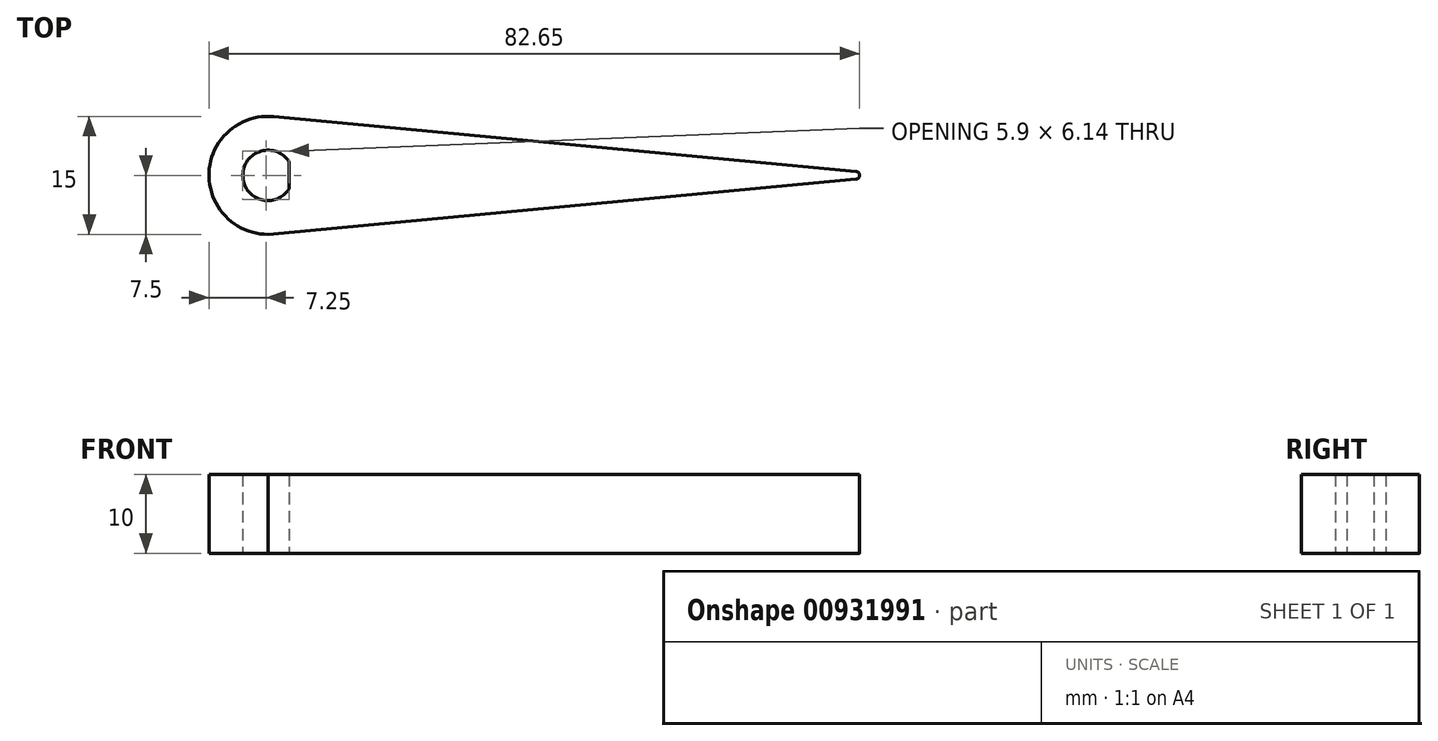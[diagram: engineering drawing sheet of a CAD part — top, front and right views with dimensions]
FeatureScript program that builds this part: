
annotation { "Feature Type Name" : "Feature", "Feature Type Description" : "" }
export const myFeature = defineFeature(function(context is Context, id is Id, definition is map)
    precondition{}
    {
        {
            var Q0;
            Q0=qCreatedBy(makeId("Top.planeOp"),FACE);
            var sketch = newSketch(context, id + "F0", { "sketchPlane" : qUnion([Q0])});
            skArc(sketch, "E0", {"start": v(2.7, 1.72) * mm, "mid": v(-3.2, 0) * mm, "end": v(2.7, -1.72) * mm});
            skLineSegment(sketch, "E1", {"start": v(2.7, 1.72) * mm, "end": v(2.7, -1.72) * mm});
            skCircle(sketch, "E2", {"center": v(0, 0) * mm, "radius": 7.5 * mm});
            skLineSegment(sketch, "E3", {"start": v(0, 0) * mm, "end": v(80, 0) * mm});
            skLineSegment(sketch, "E4", {"start": v(80, 0) * mm, "end": v(0, 7.53) * mm});
            skLineSegment(sketch, "E5", {"start": v(0, 7.53) * mm, "end": v(0, -7.5) * mm, "construction": true});
            skLineSegment(sketch, "E6", {"start": v(0, -7.5) * mm, "end": v(80, 0) * mm});
            skSolve(sketch);
        }
        {
            var Q0;
            {var subQ4=sQuery(id+"F0.wireOp",EDGE,"E0");Q0=makeQuery(id+"F0.imprint","IMPRINT",FACE,{"disambiguationData":[TD([[makeQuery(id+"F0.imprint","IMPRINT",EDGE,{"derivedFrom":subQ4}),-1.0]])]});}
            var Q1;
            {var subQ0=sQuery(id+"F0.wireOp",EDGE,"E4");var subQ1=sQuery(id+"F0.wireOp",EDGE,"E2");var subQ2=makeQuery(id+"F0.imprint","INTERSECT",VERTEX,{"derivedFrom":[subQ1,subQ0]});Q1=makeQuery(id+"F0.imprint","IMPRINT",FACE,{"disambiguationData":[TD([[makeQuery(id+"F0.imprint","IMPRINT",EDGE,{"disambiguationData":[TD([[subQ2,1.0]])],"derivedFrom":subQ1}),-1.0]])]});}
            var Q2;
            {var subQ0=sQuery(id+"F0.wireOp",EDGE,"E3");var subQ1=sQuery(id+"F0.wireOp",EDGE,"E2");var subQ2=makeQuery(id+"F0.imprint","INTERSECT",VERTEX,{"derivedFrom":[subQ1,subQ0]});Q2=makeQuery(id+"F0.imprint","IMPRINT",FACE,{"disambiguationData":[TD([[makeQuery(id+"F0.imprint","IMPRINT",EDGE,{"disambiguationData":[TD([[subQ2,1.0]])],"derivedFrom":subQ1}),-1.0]])]});}
            extrude(context, id + "F1", {"entities" : qUnion([Q0, Q1, Q2]), "depth" : 10 * mm, "offsetDistance" : 25 * mm});
        }
        {
            var Q0;
            Q0=makeQuery(id+"F1.opExtrude","SWEPT_EDGE",EDGE,{"disambiguationData":[OSD([sQuery(id+"F0.wireOp",EDGE,"E3"),sQuery(id+"F0.wireOp",EDGE,"E4"),sQuery(id+"F0.wireOp",EDGE,"E6")])]});
            fillet(context, id + "F2", {"entities" : qUnion([Q0]), "radius" : 0.5 * mm, "tangentPropagation" : true, "allowEdgeOverflow" : false});
        }
    });
